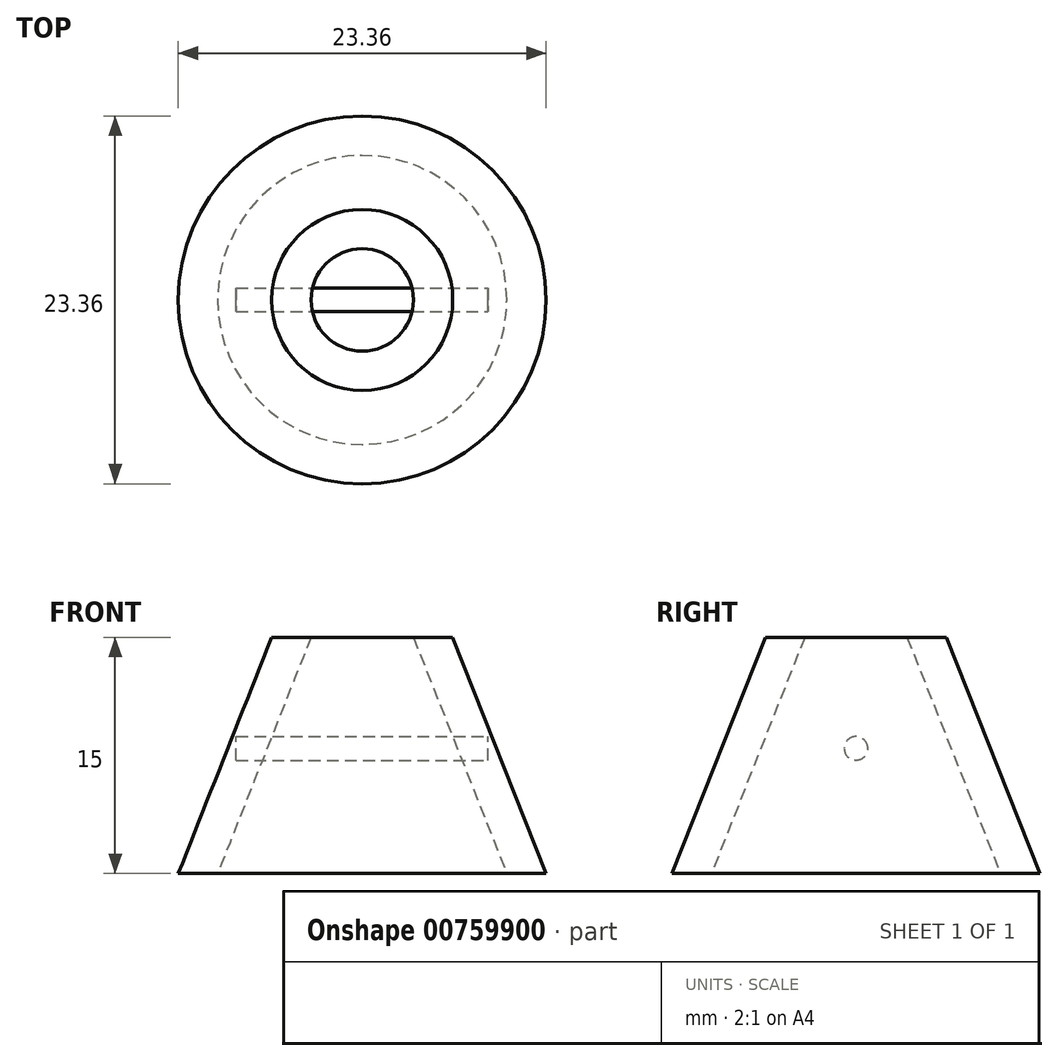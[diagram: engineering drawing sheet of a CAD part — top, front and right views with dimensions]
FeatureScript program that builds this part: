
annotation { "Feature Type Name" : "Feature", "Feature Type Description" : "" }
export const myFeature = defineFeature(function(context is Context, id is Id, definition is map)
    precondition{}
    {
        {
            var Q0;
            Q0=qCreatedBy(makeId("Front.planeOp"),FACE);
            var sketch = newSketch(context, id + "F0", { "sketchPlane" : qUnion([Q0])});
            skLineSegment(sketch, "E0", {"start": v(0, 0) * mm, "end": v(0, 15) * mm});
            skLineSegment(sketch, "E1", {"start": v(3.25, 15) * mm, "end": v(5.75, 15) * mm});
            skLineSegment(sketch, "E2", {"start": v(5.75, 15) * mm, "end": v(11.68, 0) * mm});
            skLineSegment(sketch, "E3", {"start": v(3.25, 15) * mm, "end": v(9.18, 0) * mm});
            skLineSegment(sketch, "E4", {"start": v(9.18, 0) * mm, "end": v(11.68, 0) * mm});
            skSolve(sketch);
        }
        {
            var Q0;
            Q0=qCreatedBy(makeId("Front.planeOp"),FACE);
            var sketch = newSketch(context, id + "F1", { "sketchPlane" : qUnion([Q0])});
            skLineSegment(sketch, "E5.bottom", {"start": v(8, 7.2) * mm, "end": v(-8, 7.2) * mm});
            skLineSegment(sketch, "E5.top", {"start": v(8, 7.95) * mm, "end": v(-8, 7.95) * mm});
            skLineSegment(sketch, "E5.left", {"start": v(8, 7.2) * mm, "end": v(8, 7.95) * mm});
            skLineSegment(sketch, "E5.right", {"start": v(-8, 7.2) * mm, "end": v(-8, 7.95) * mm});
            skLineSegment(sketch, "E6", {"start": v(0, 0) * mm, "end": v(0, 7.2) * mm, "construction": true});
            skSolve(sketch);
        }
        {
            var Q0;
            Q0=makeQuery(id+"F1.imprint","IMPRINT",FACE,{"disambiguationData":[TD([[makeQuery(id+"F1.imprint","IMPRINT",EDGE,{"derivedFrom":sQuery(id+"F1.wireOp",EDGE,"E5.bottom")}),-1.0]])]});
            var Q1;
            Q1=sQuery(id+"F1.wireOp",EDGE,"E5.top");
            revolve(context, id + "F2", {"surfaceOperationType" : NewSurfaceOperationType.NEW, "entities" : qUnion([Q0]), "axis" : qUnion([Q1]), "revolveType" : RevolveType.FULL});
        }
        {
            var Q0;
            Q0=makeQuery(id+"F0.imprint","IMPRINT",FACE,{"disambiguationData":[TD([[makeQuery(id+"F0.imprint","IMPRINT",EDGE,{"derivedFrom":sQuery(id+"F0.wireOp",EDGE,"E1")}),-1.0]])]});
            var Q1;
            Q1=sQuery(id+"F0.wireOp",EDGE,"E0");
            revolve(context, id + "F3", {"surfaceOperationType" : NewSurfaceOperationType.NEW, "entities" : qUnion([Q0]), "axis" : qUnion([Q1]), "revolveType" : RevolveType.FULL});
        }
    });
